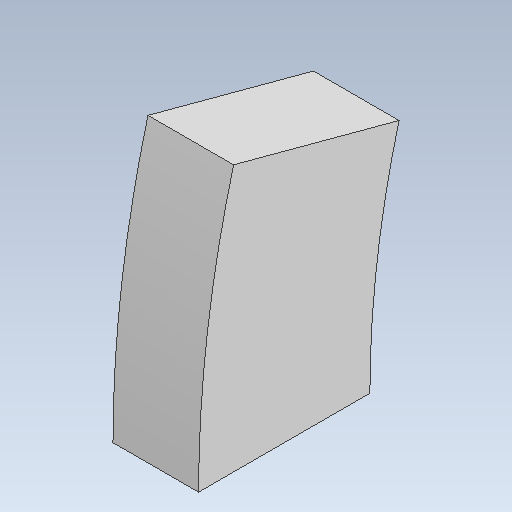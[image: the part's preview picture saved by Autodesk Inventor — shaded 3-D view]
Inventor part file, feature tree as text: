
AUTODESK INVENTOR PART (.ipt)
format: ipt  version: 2021 (Build 250183000, 183)  size: 105,984 bytes
history: native  units: mm
features: extrude x1
ambient origin geometry x8: Origin, YZ Plane, XZ Plane, XY Plane, X Axis, Y Axis, Z Axis, Center Point
bodies: Solid1 (feature_tree)
feature tree (1):
  extrude  "Extrusion1"  Depth=300.0mm
